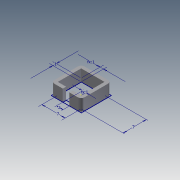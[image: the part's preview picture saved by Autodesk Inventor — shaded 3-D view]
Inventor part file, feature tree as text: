
AUTODESK INVENTOR PART (.ipt)
format: ipt  version: 2011 (Build 150239000, 239)  size: 91,648 bytes
history: native  units: mm
features: extrude x1, fillet x1, sketch x1
ambient origin geometry x8: Origin, YZ Plane, XZ Plane, XY Plane, X Axis, Y Axis, Z Axis, Center Point
bodies: Solid1 (feature_tree)
feature tree (3):
  extrude  "Extrusion1"  Depth=1.0mm
  fillet  "Fillet1"  Radius=7.0mm
  sketch  "Sketch1"  dims[d0=1.0mm d1=1.0mm d2=7.0mm d3=7.0mm d4=2.0mm d5=1.0mm d6=3.5mm d7=0.0mm d8=1.0mm]
